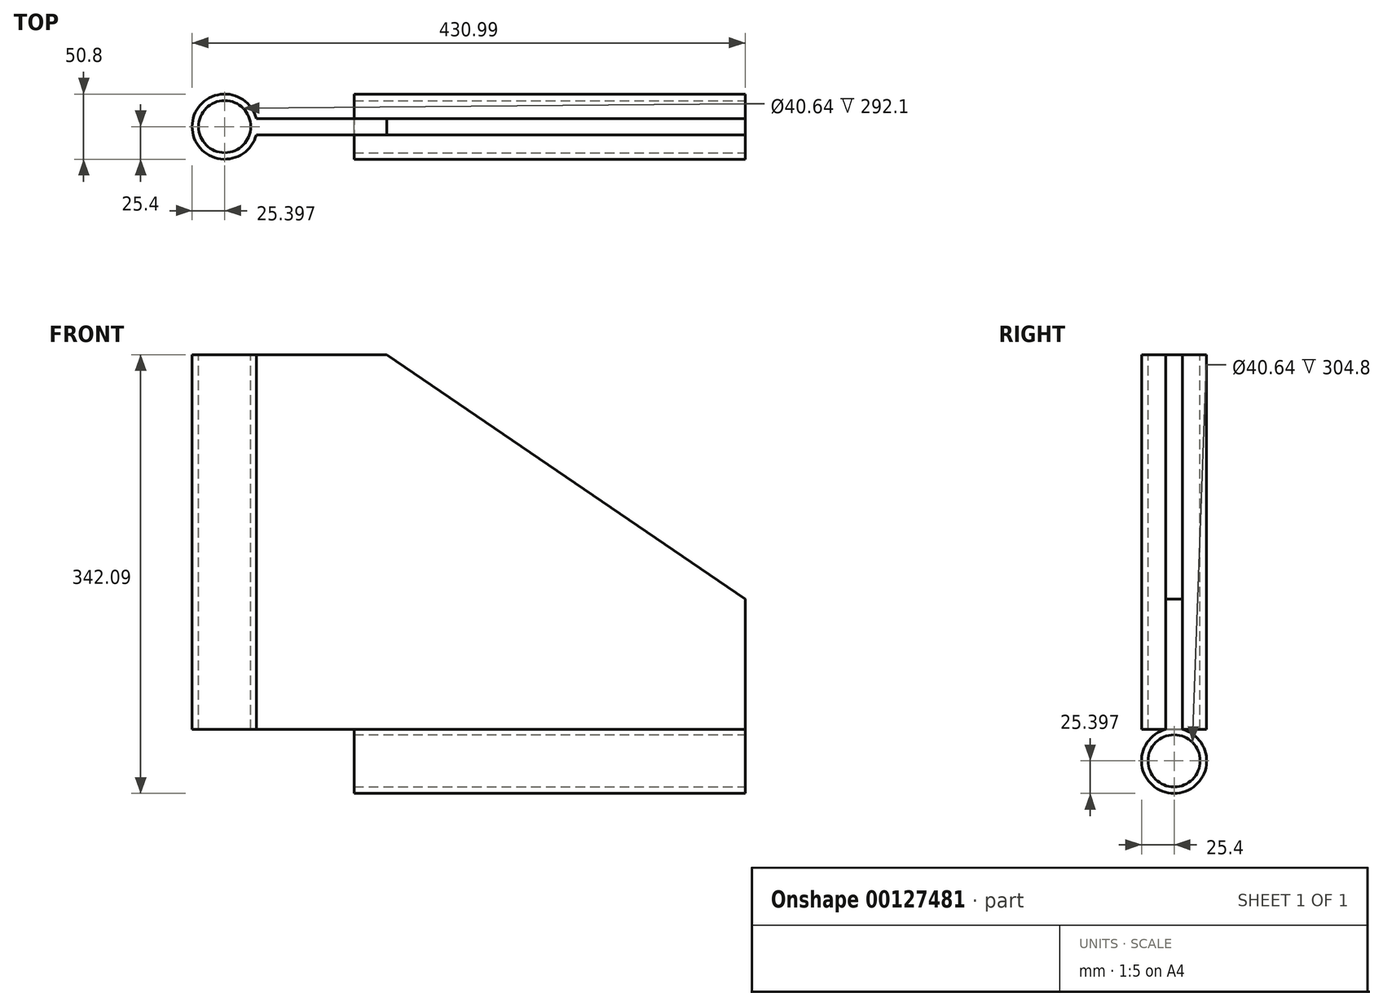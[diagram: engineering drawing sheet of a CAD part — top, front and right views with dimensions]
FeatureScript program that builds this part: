
annotation { "Feature Type Name" : "Feature", "Feature Type Description" : "" }
export const myFeature = defineFeature(function(context is Context, id is Id, definition is map)
    precondition{}
    {
        {
            var Q0;
            Q0=qCreatedBy(makeId("Front.planeOp"),FACE);
            var sketch = newSketch(context, id + "F0", { "sketchPlane" : qUnion([Q0])});
            skLineSegment(sketch, "E0", {"start": v(0, 0) * mm, "end": v(0, -292.1) * mm});
            skLineSegment(sketch, "E1", {"start": v(0, -292.1) * mm, "end": v(381, -292.1) * mm});
            skLineSegment(sketch, "E2", {"start": v(381, -292.1) * mm, "end": v(381, -190.5) * mm});
            skLineSegment(sketch, "E3", {"start": v(381, -190.5) * mm, "end": v(101.6, 0) * mm});
            skLineSegment(sketch, "E4", {"start": v(101.6, 0) * mm, "end": v(0, 0) * mm});
            skSolve(sketch);
        }
        {
            var Q0;
            Q0=makeQuery(id+"F0.imprint","IMPRINT",FACE,{"disambiguationData":[TD([[makeQuery(id+"F0.imprint","IMPRINT",EDGE,{"derivedFrom":sQuery(id+"F0.wireOp",EDGE,"E0")}),1.0]])]});
            extrude(context, id + "F1", {"entities" : qUnion([Q0]), "endBound" : BoundingType.SYMMETRIC, "depth" : 12.7 * mm});
        }
        {
            var Q0;
            Q0=qCreatedBy(makeId("Top.planeOp"),FACE);
            var sketch = newSketch(context, id + "F2", { "sketchPlane" : qUnion([Q0])});
            skLineSegment(sketch, "E5", {"start": v(0.8, 0) * mm, "end": v(-24.6, 0) * mm, "construction": true});
            skCircle(sketch, "E6", {"center": v(-24.6, 0) * mm, "radius": 25.4 * mm});
            skCircle(sketch, "E7", {"center": v(-24.6, 0) * mm, "radius": 20.32 * mm});
            skLineSegment(sketch, "E8", {"start": v(-24.6, 20.32) * mm, "end": v(-24.6, 25.4) * mm, "construction": true});
            skSolve(sketch);
        }
        {
            var Q0;
            Q0=makeQuery(id+"F2.imprint","IMPRINT",FACE,{"disambiguationData":[TD([[makeQuery(id+"F2.imprint","IMPRINT",EDGE,{"derivedFrom":sQuery(id+"F2.wireOp",EDGE,"E6")}),1.0]])]});
            var Q1;
            Q1=makeQuery(id+"F1.opExtrude","SWEPT_FACE",FACE,{"disambiguationData":[OSD([sQuery(id+"F0.wireOp",EDGE,"E1")])]});
            extrude(context, id + "F3", {"entities" : qUnion([Q0]), "operationType" : NewBodyOperationType.ADD, "endBound" : BoundingType.UP_TO_SURFACE, "oppositeDirection" : true, "endBoundEntityFace" : qUnion([Q1]), "depth" : 25.4 * mm});
        }
        {
            var Q0;
            Q0=makeQuery(id+"F1.opExtrude","SWEPT_FACE",FACE,{"disambiguationData":[OSD([sQuery(id+"F0.wireOp",EDGE,"E2")])]});
            var sketch = newSketch(context, id + "F4", { "sketchPlane" : qUnion([Q0])});
            skCircle(sketch, "E9", {"center": v(0, -316.7) * mm, "radius": 20.32 * mm});
            skCircle(sketch, "E10", {"center": v(0, -316.7) * mm, "radius": 25.4 * mm});
            skLineSegment(sketch, "E11", {"start": v(20.32, -316.7) * mm, "end": v(25.4, -316.7) * mm, "construction": true});
            skSolve(sketch);
        }
        {
            var Q0;
            Q0=makeQuery(id+"F4.imprint","IMPRINT",FACE,{"disambiguationData":[TD([[makeQuery(id+"F4.imprint","IMPRINT",EDGE,{"derivedFrom":sQuery(id+"F4.wireOp",EDGE,"E9")}),-1.0]])]});
            var Q1;
            Q1=makeQuery(id+"F1.opExtrude","SWEPT_FACE",FACE,{"disambiguationData":[OSD([sQuery(id+"F0.wireOp",EDGE,"E0")])]});
            extrude(context, id + "F5", {"entities" : qUnion([Q0]), "operationType" : NewBodyOperationType.ADD, "oppositeDirection" : true, "endBoundEntityFace" : qUnion([Q1]), "depth" : 304.8 * mm});
        }
    });
